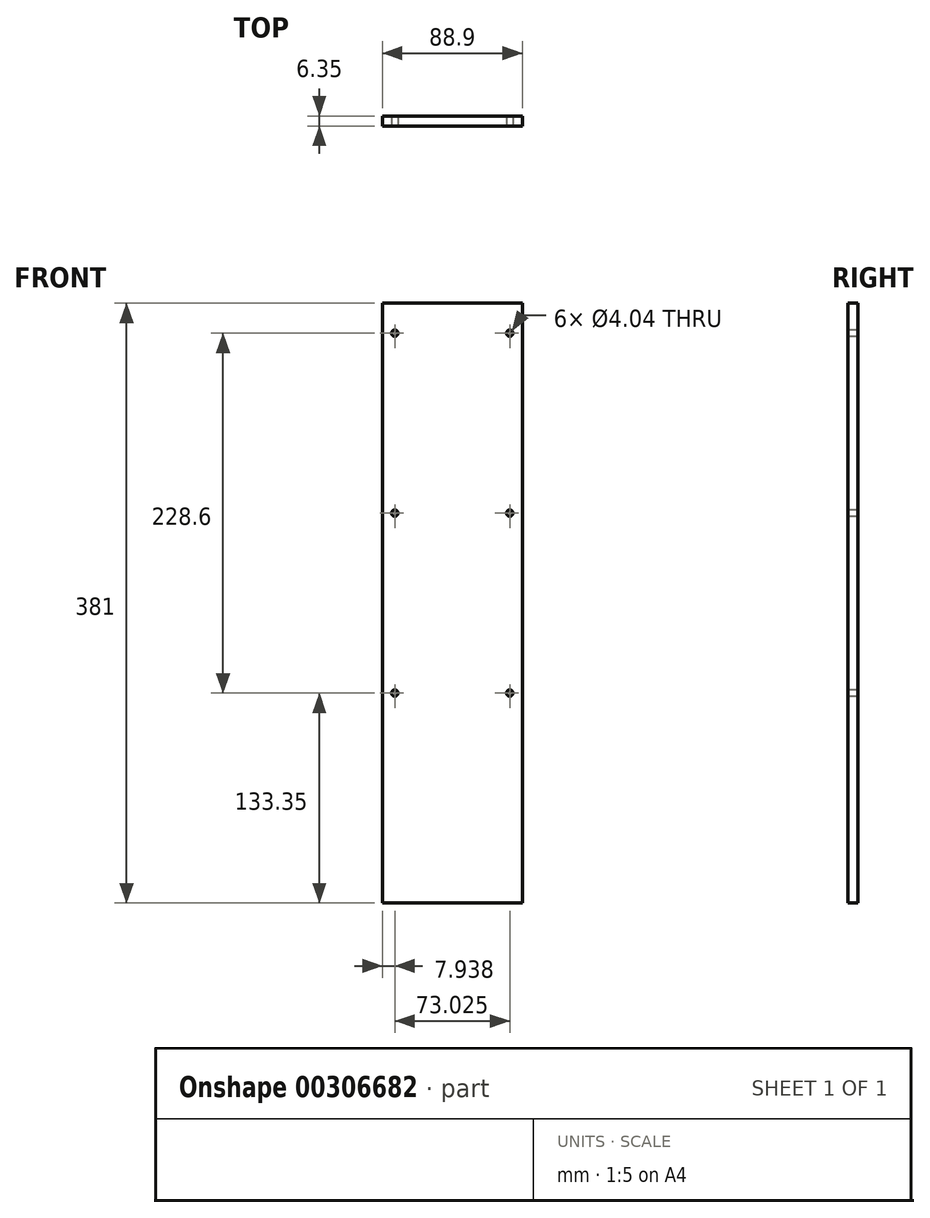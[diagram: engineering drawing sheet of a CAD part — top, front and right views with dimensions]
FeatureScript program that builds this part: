
annotation { "Feature Type Name" : "Feature", "Feature Type Description" : "" }
export const myFeature = defineFeature(function(context is Context, id is Id, definition is map)
    precondition{}
    {
        {
            var Q0;
            Q0=qCreatedBy(makeId("Front.planeOp"),FACE);
            var sketch = newSketch(context, id + "F0", { "sketchPlane" : qUnion([Q0])});
            skLineSegment(sketch, "E0.bottom", {"start": v(-44.45, 190.5) * mm, "end": v(44.45, 190.5) * mm});
            skLineSegment(sketch, "E0.top", {"start": v(-44.45, -190.5) * mm, "end": v(44.45, -190.5) * mm});
            skLineSegment(sketch, "E0.left", {"start": v(-44.45, 190.5) * mm, "end": v(-44.45, -190.5) * mm});
            skLineSegment(sketch, "E0.right", {"start": v(44.45, 190.5) * mm, "end": v(44.45, -190.5) * mm});
            skPoint(sketch, "E0.middle", {"position": v(0, 0) * mm});
            skSolve(sketch);
        }
        {
            var Q0;
            Q0=makeQuery(id+"F0.imprint","IMPRINT",FACE,{"disambiguationData":[TD([[makeQuery(id+"F0.imprint","IMPRINT",EDGE,{"derivedFrom":sQuery(id+"F0.wireOp",EDGE,"E0.bottom")}),-1.0]])]});
            extrude(context, id + "F1", {"entities" : qUnion([Q0]), "depth" : 6.35 * mm});
        }
        {
            var Q0;
            Q0=makeQuery(id+"F1.opExtrude","CAP_FACE",FACE,{"disambiguationData":[OSD([sQuery(id+"F0.wireOp",EDGE,"E0.bottom"),sQuery(id+"F0.wireOp",EDGE,"E0.top"),sQuery(id+"F0.wireOp",EDGE,"E0.left"),sQuery(id+"F0.wireOp",EDGE,"E0.right")])],"isStart":false});
            var sketch = newSketch(context, id + "F2", { "sketchPlane" : qUnion([Q0])});
            skPoint(sketch, "E1", {"position": v(-36.51, 171.45) * mm});
            skPoint(sketch, "E2", {"position": v(-36.51, 57.15) * mm});
            skPoint(sketch, "E3", {"position": v(36.51, 57.15) * mm});
            skPoint(sketch, "E4", {"position": v(36.51, 171.45) * mm});
            skLineSegment(sketch, "E5", {"start": v(0, 0) * mm, "end": v(0, 102.92) * mm});
            skPoint(sketch, "E6", {"position": v(36.51, -57.15) * mm});
            skPoint(sketch, "E7", {"position": v(-36.51, -57.15) * mm});
            skSolve(sketch);
        }
        {
            var Q0;
            Q0=sQuery(id+"F2.wireOp",VERTEX,"E1");
            var Q1;
            Q1=sQuery(id+"F2.wireOp",VERTEX,"E4");
            var Q2;
            Q2=sQuery(id+"F2.wireOp",VERTEX,"E3");
            var Q3;
            Q3=sQuery(id+"F2.wireOp",VERTEX,"E2");
            var Q4;
            Q4=sQuery(id+"F2.wireOp",VERTEX,"E7");
            var Q5;
            Q5=sQuery(id+"F2.wireOp",VERTEX,"E6");
            var Q6;
            Q6=makeQuery(id+"F1.opExtrude","SWEPT_BODY",BODY,{"disambiguationData":[OSD([sQuery(id+"F0.wireOp",EDGE,"E0.bottom"),sQuery(id+"F0.wireOp",EDGE,"E0.top"),sQuery(id+"F0.wireOp",EDGE,"E0.left"),sQuery(id+"F0.wireOp",EDGE,"E0.right")])]});
            hole(context, id + "F3", {"style" : HoleStyle.SIMPLE, "endStyle" : HoleEndStyle.THROUGH, "standardTappedOrClearance" : lookupTablePath({ "standard" : "ANSI", "engagement" : "75%", "pitch" : "32 tpi", "size" : "#10", "type" : "Tapped" }), "standardBlindInLast" : lookupTablePath({ "standard" : "ANSI", "engagement" : "75%", "pitch" : "32 tpi", "size" : "#10", "type" : "Tapped" }), "holeDiameter" : 4.04 * mm, "showTappedDepth" : true, "tappedDepth" : 12.7 * mm, "tapClearance" : 3, "locations" : qUnion([Q0, Q1, Q2, Q3, Q4, Q5]), "scope" : qUnion([Q6]), "majorDiameter" : 4.83 * mm});
        }
    });
